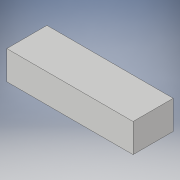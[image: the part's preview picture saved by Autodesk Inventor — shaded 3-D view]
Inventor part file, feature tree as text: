
AUTODESK INVENTOR PART (.ipt)
format: ipt  version: 2018.2 (Build 222227000, 227)  size: 87,552 bytes
history: native  units: in
note: dims shown in document units (in); Inventor stores cm internally (conversion verified against a paired STEP export)
features: extrude x1, sketch x1
ambient origin geometry x8: Origin, YZ Plane, XZ Plane, XY Plane, X Axis, Y Axis, Z Axis, Center Point
bodies: Solid1 (feature_tree)
feature tree (2):
  extrude  "Extrusion1"  Depth=0.9843in
  sketch  "Sketch1"  dims[d0=4.3307in d1=0.9843in d2=1.378in d3=0.0in]
